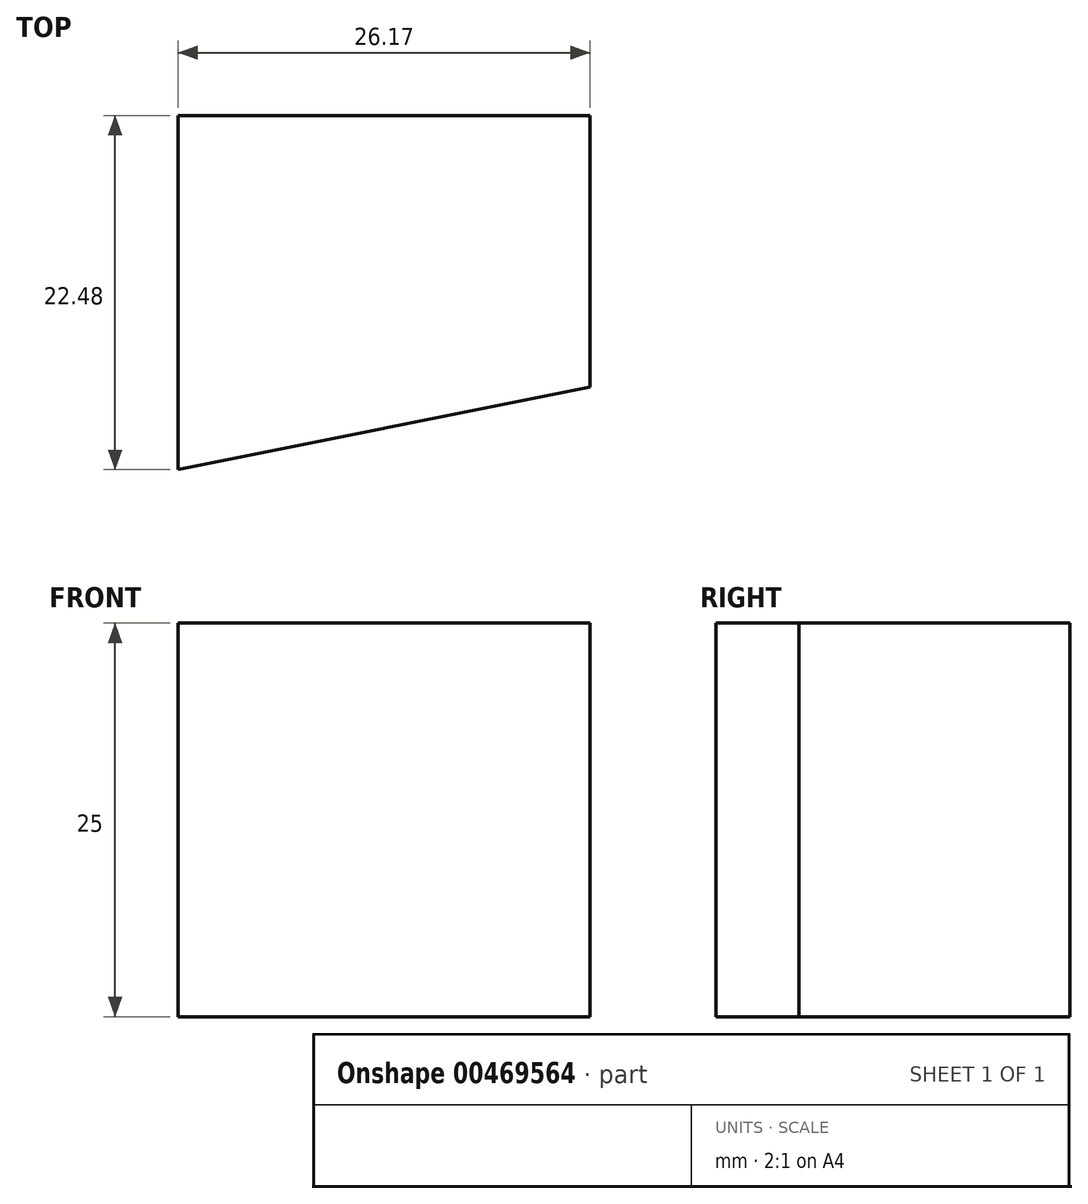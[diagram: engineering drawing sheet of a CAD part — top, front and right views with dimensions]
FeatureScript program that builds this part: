
annotation { "Feature Type Name" : "Feature", "Feature Type Description" : "" }
export const myFeature = defineFeature(function(context is Context, id is Id, definition is map)
    precondition{}
    {
        {
            var Q0;
            Q0=qCreatedBy(makeId("Top.planeOp"),FACE);
            var sketch = newSketch(context, id + "F0", { "sketchPlane" : qUnion([Q0])});
            skLineSegment(sketch, "E0", {"start": v(26.17, 0) * mm, "end": v(26.17, 29.65) * mm});
            skLineSegment(sketch, "E1", {"start": v(26.17, 0) * mm, "end": v(144.12, 29.65) * mm});
            skLineSegment(sketch, "E2", {"start": v(144.12, 29.65) * mm, "end": v(0, -36.6) * mm});
            skLineSegment(sketch, "E3", {"start": v(0, -36.6) * mm, "end": v(0, 0) * mm});
            skLineSegment(sketch, "E4", {"start": v(0, 0) * mm, "end": v(-121.59, 0) * mm});
            skLineSegment(sketch, "E5", {"start": v(-121.59, 0) * mm, "end": v(26.17, 29.65) * mm});
            skSolve(sketch);
        }
        {
            var Q0;
            Q0=makeQuery(id+"F0.imprint","IMPRINT",FACE,{"disambiguationData":[TD([[makeQuery(id+"F0.imprint","IMPRINT",EDGE,{"derivedFrom":sQuery(id+"F0.wireOp",EDGE,"E0")}),1.0]])]});
            var sketch = newSketch(context, id + "F1", { "sketchPlane" : qUnion([Q0])});
            skLineSegment(sketch, "E6", {"start": v(0, 24.68) * mm, "end": v(0, 46.88) * mm});
            skLineSegment(sketch, "E7", {"start": v(0, 46.88) * mm, "end": v(26.17, 46.88) * mm});
            skLineSegment(sketch, "E8", {"start": v(26.17, 46.88) * mm, "end": v(26.17, 21.7) * mm});
            skLineSegment(sketch, "E9", {"start": v(26.17, 21.7) * mm, "end": v(0, 21.7) * mm});
            skLineSegment(sketch, "E10", {"start": v(0, 21.7) * mm, "end": v(0, 24.68) * mm});
            skSolve(sketch);
        }
        {
            var Q0;
            {var subQ6=sQuery(id+"F1.wireOp",EDGE,"E6");Q0=makeQuery(id+"F1.imprint","IMPRINT",FACE,{"disambiguationData":[TD([[makeQuery(id+"F1.imprint","IMPRINT",EDGE,{"derivedFrom":subQ6}),-1.0]])]});}
            extrude(context, id + "F2", {"entities" : qUnion([Q0]), "depth" : 25 * mm});
        }
    });
